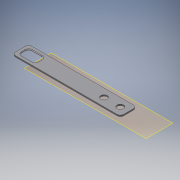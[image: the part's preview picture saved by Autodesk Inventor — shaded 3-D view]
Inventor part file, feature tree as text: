
AUTODESK INVENTOR PART (.ipt)
format: ipt  version: 2016 SP2 (Build 200236200, 236)  size: 143,872 bytes
history: native  units: mm
features: reference x3, fillet x2, plane x1, extrude x1, sketch x1
ambient origin geometry x8: Origin, YZ Plane, XZ Plane, XY Plane, X Axis, Y Axis, Z Axis, Center Point
bodies: Volumenkörper1 (feature_tree)
feature tree (8):
  plane  "Arbeitsebene1"
  extrude  "Extrusion1"  Depth=25.0mm
  fillet  "Rundung1"  Radius=12.5mm
  fillet  "Rundung2"  Radius=5.0mm
  sketch  "Skizze1"  dims[d0=12.5mm d1=25.0mm d2=12.5mm d3=5.0mm d4=5.0mm d5=5.0mm d6=25.0mm d7=5.0mm d8=15.0mm d9=2.0mm d10=0.0mm d11=5.0mm d12=1.0mm]
  reference  "Referenz2"
  reference  "Referenz3"
  reference  "Referenz4"
